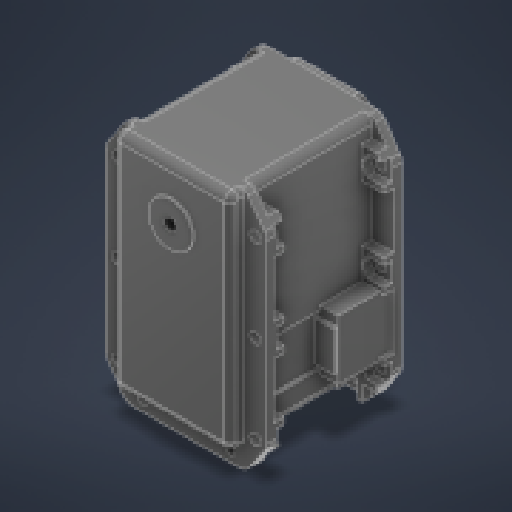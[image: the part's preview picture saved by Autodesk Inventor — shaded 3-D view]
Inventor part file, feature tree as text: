
AUTODESK INVENTOR PART (.ipt)
format: ipt  version: 2024 (Build 280153000, 153)  size: 602,624 bytes
history: native  units: mm
features: other x6, projected_geometry x4, extrude x3, sketch x2
ambient origin geometry x8: Origin, YZ Plane, XZ Plane, XY Plane, X Axis, Y Axis, Z Axis, Center Point
bodies: Body1 (feature_tree)
feature tree (15):
  other  "솔리드1"
  extrude  "돌출1"  Depth=22.0mm
  other  "작업 평면1"
  other  "작업 평면2"
  other  "작업 평면3"
  extrude  "돌출2"  Depth=2.5mm
  extrude  "돌출3"  Depth=80.0mm TaperAngle=360.0deg
  other  "스레드1"
  projected_geometry  "투영된 루프1"
  sketch  "스케치2"
  projected_geometry  "투영된 루프2"
  projected_geometry  "투영된 루프3"
  sketch  "스케치3"
  projected_geometry  "투영된 루프4"
  other  "기준1"
